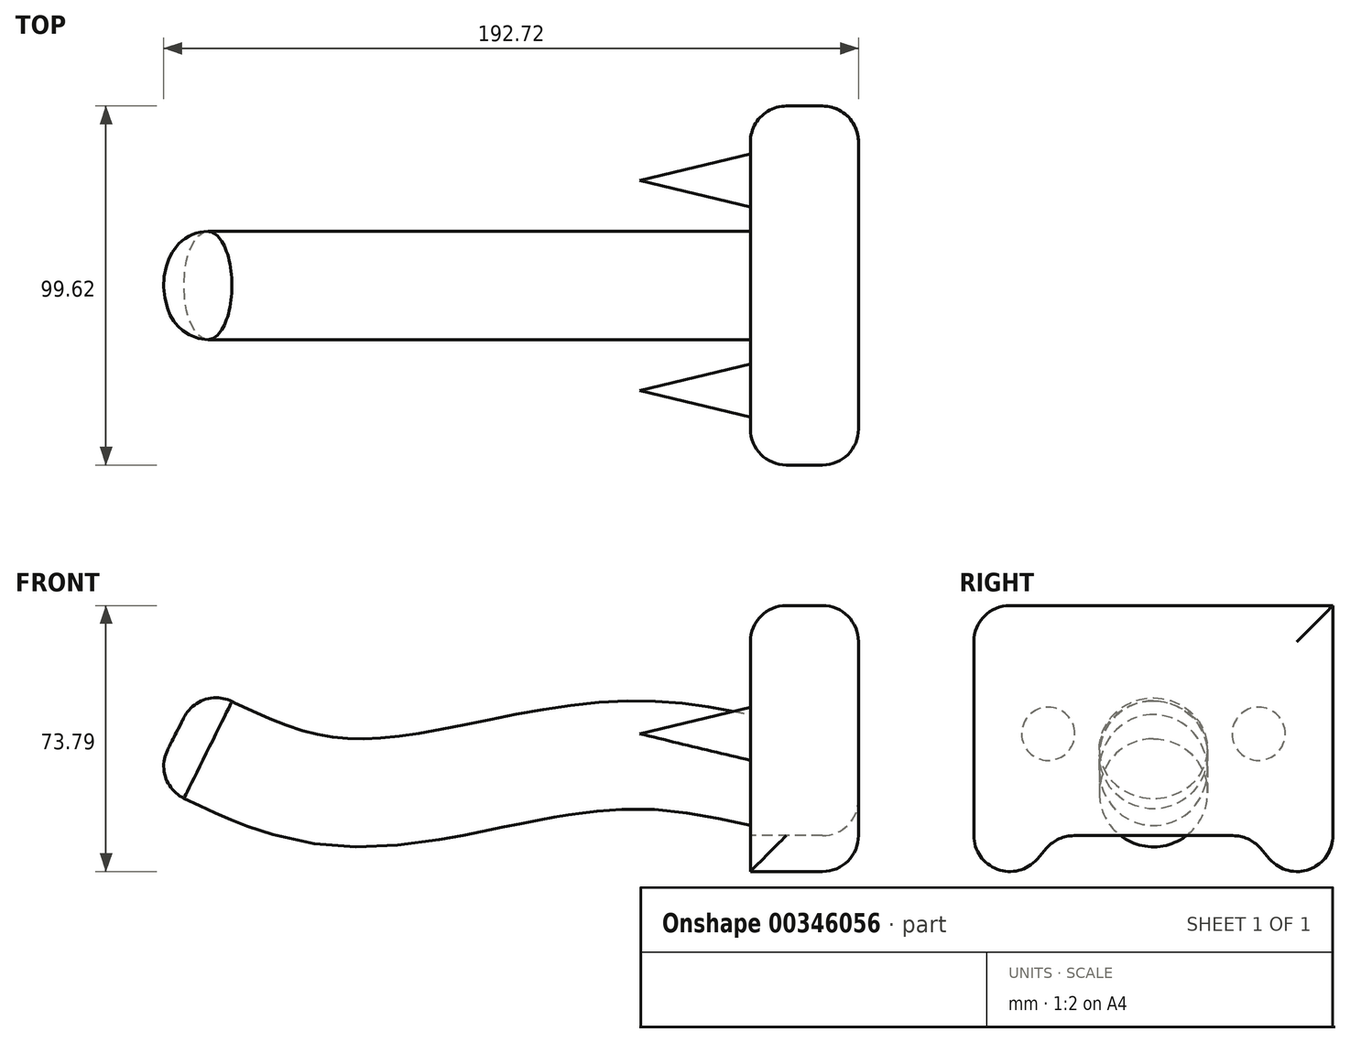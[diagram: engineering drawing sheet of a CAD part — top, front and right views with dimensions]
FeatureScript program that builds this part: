
annotation { "Feature Type Name" : "Feature", "Feature Type Description" : "" }
export const myFeature = defineFeature(function(context is Context, id is Id, definition is map)
    precondition{}
    {
        {
            var Q0;
            Q0=qCreatedBy(makeId("Right.planeOp"),FACE);
            var sketch = newSketch(context, id + "F0", { "sketchPlane" : qUnion([Q0])});
            skLineSegment(sketch, "E0", {"start": v(0, -28.27) * mm, "end": v(26.56, -28.27) * mm});
            skLineSegment(sketch, "E1", {"start": v(26.56, -28.27) * mm, "end": v(49.8, -54.84) * mm});
            skLineSegment(sketch, "E2", {"start": v(49.8, -54.84) * mm, "end": v(49.8, 35.57) * mm});
            skLineSegment(sketch, "E3", {"start": v(49.8, 35.57) * mm, "end": v(0, 35.57) * mm});
            skLineSegment(sketch, "E4.MirrorCS", {"start": v(0, -28.27) * mm, "end": v(-26.56, -28.27) * mm});
            skLineSegment(sketch, "E5.MirrorCS", {"start": v(-49.8, 35.57) * mm, "end": v(0, 35.57) * mm});
            skLineSegment(sketch, "E6.MirrorCS", {"start": v(-26.56, -28.27) * mm, "end": v(-49.8, -54.84) * mm});
            skLineSegment(sketch, "E7.MirrorCS", {"start": v(-49.8, -54.84) * mm, "end": v(-49.8, 35.57) * mm});
            skSolve(sketch);
        }
        {
            var Q0;
            Q0=makeQuery(id+"F0.imprint","IMPRINT",FACE,{"disambiguationData":[TD([[makeQuery(id+"F0.imprint","IMPRINT",EDGE,{"derivedFrom":sQuery(id+"F0.wireOp",EDGE,"E0")}),1.0]])]});
            extrude(context, id + "F1", {"entities" : qUnion([Q0]), "depth" : 30 * mm});
        }
        {
            var Q0;
            Q0=qCreatedBy(makeId("Front.planeOp"),FACE);
            var sketch = newSketch(context, id + "F2", { "sketchPlane" : qUnion([Q0])});
            skFitSpline(sketch, "E8", {"points": [v(11.8, -12.91) * mm, v(-35.42, -5.9) * mm, v(-90.03, -14.76) * mm, v(-125.09, -14.4) * mm, v(-159.4, 0) * mm], "startDerivative": vector(-174.02, 43.3) * mm, "endDerivative": vector(-148.88, 75.43) * mm});
            skSolve(sketch);
        }
        {
            var Q0;
            Q0=sQuery(id+"F2.wireOp",VERTEX,"E8.4.internal");
            var Q1;
            Q1=sQuery(id+"F2.wireOp",EDGE,"E8");
            cPlane(context, id + "F3", {"entities" : qUnion([Q0, Q1]), "cplaneType" : CPlaneType.CURVE_POINT, "offset" : 25 * mm, "width" : 150 * mm, "height" : 150 * mm});
        }
        {
            var Q0;
            Q0=qCreatedBy(id+"F3.planeOp",FACE);
            var sketch = newSketch(context, id + "F4", { "sketchPlane" : qUnion([Q0])});
            skPoint(sketch, "E9.0", {"position": v(0, -72.05) * mm});
            skCircle(sketch, "E10", {"center": v(0, -72.05) * mm, "radius": 15 * mm});
            skSolve(sketch);
        }
        {
            var Q0;
            Q0=makeQuery(id+"F4.imprint","IMPRINT",FACE,{"disambiguationData":[TD([[makeQuery(id+"F4.imprint","IMPRINT",EDGE,{"derivedFrom":sQuery(id+"F4.wireOp",EDGE,"E10")}),1.0]])]});
            var Q1;
            Q1=sQuery(id+"F2.wireOp",EDGE,"E8");
            sweep(context, id + "F5", {"operationType" : NewBodyOperationType.ADD, "profiles" : qUnion([Q0]), "path" : qUnion([Q1])});
        }
        {
            var Q0;
            Q0=qCreatedBy(makeId("Top.planeOp"),FACE);
            var sketch = newSketch(context, id + "F6", { "sketchPlane" : qUnion([Q0])});
            skLineSegment(sketch, "E11.0", {"start": v(0, 26.56) * mm, "end": v(0, 49.8) * mm});
            skLineSegment(sketch, "E12.0", {"start": v(0, 26.56) * mm, "end": v(0, -26.56) * mm});
            skLineSegment(sketch, "E13", {"start": v(0, 29.18) * mm, "end": v(-30.72, 29.18) * mm});
            skLineSegment(sketch, "E14", {"start": v(-30.72, 29.18) * mm, "end": v(0, 36.56) * mm});
            skLineSegment(sketch, "E15", {"start": v(0, 36.56) * mm, "end": v(0, 29.18) * mm});
            skSolve(sketch);
        }
        {
            var Q0;
            Q0=makeQuery(id+"F6.imprint","IMPRINT",FACE,{"disambiguationData":[TD([[makeQuery(id+"F6.imprint","IMPRINT",EDGE,{"derivedFrom":sQuery(id+"F6.wireOp",EDGE,"E13")}),-1.0]])]});
            var Q1;
            Q1=sQuery(id+"F6.wireOp",EDGE,"E13");
            revolve(context, id + "F7", {"operationType" : NewBodyOperationType.ADD, "entities" : qUnion([Q0]), "axis" : qUnion([Q1]), "revolveType" : RevolveType.FULL});
        }
        {
            var Q0;
            Q0=makeQuery(id+"F1.opExtrude","SWEPT_BODY",BODY,{"disambiguationData":[OSD([sQuery(id+"F0.wireOp",EDGE,"E0"),sQuery(id+"F0.wireOp",EDGE,"E1"),sQuery(id+"F0.wireOp",EDGE,"E2"),sQuery(id+"F0.wireOp",EDGE,"E3"),sQuery(id+"F0.wireOp",EDGE,"E4.MirrorCS"),sQuery(id+"F0.wireOp",EDGE,"E5.MirrorCS"),sQuery(id+"F0.wireOp",EDGE,"E6.MirrorCS"),sQuery(id+"F0.wireOp",EDGE,"E7.MirrorCS")])]});
            var Q1;
            Q1=qCreatedBy(makeId("Front.planeOp"),FACE);
            mirror(context, id + "F8", {"operationType" : NewBodyOperationType.ADD, "entities" : qUnion([Q0]), "mirrorPlane" : qUnion([Q1])});
        }
        {
            var Q0;
            Q0=makeQuery(id+"F5.opSweep","CAP_EDGE",EDGE,{"disambiguationData":[OSD([sQuery(id+"F2.wireOp",VERTEX,"E8.end"),sQuery(id+"F4.wireOp",EDGE,"E10")])],"isStart":true});
            var Q1;
            Q1=makeQuery(id+"F1.opExtrude","SWEPT_EDGE",EDGE,{"disambiguationData":[OSD([sQuery(id+"F0.wireOp",EDGE,"E5.MirrorCS"),sQuery(id+"F0.wireOp",EDGE,"E7.MirrorCS")])]});
            var Q2;
            Q2=makeQuery(id+"F1.opExtrude","CAP_EDGE",EDGE,{"disambiguationData":[OSD([sQuery(id+"F0.wireOp",EDGE,"E7.MirrorCS")])],"isStart":true});
            var Q3;
            Q3=makeQuery(id+"F1.opExtrude","CAP_EDGE",EDGE,{"disambiguationData":[OSD([sQuery(id+"F0.wireOp",EDGE,"E3"),sQuery(id+"F0.wireOp",EDGE,"E5.MirrorCS")])],"isStart":true});
            var Q4;
            Q4=makeQuery(id+"F1.opExtrude","CAP_EDGE",EDGE,{"disambiguationData":[OSD([sQuery(id+"F0.wireOp",EDGE,"E2")])],"isStart":true});
            var Q5;
            Q5=makeQuery(id+"F1.opExtrude","CAP_EDGE",EDGE,{"disambiguationData":[OSD([sQuery(id+"F0.wireOp",EDGE,"E7.MirrorCS")])],"isStart":false});
            var Q6;
            Q6=makeQuery(id+"F1.opExtrude","CAP_EDGE",EDGE,{"disambiguationData":[OSD([sQuery(id+"F0.wireOp",EDGE,"E2")])],"isStart":false});
            var Q7;
            Q7=makeQuery(id+"F1.opExtrude","CAP_EDGE",EDGE,{"disambiguationData":[OSD([sQuery(id+"F0.wireOp",EDGE,"E3"),sQuery(id+"F0.wireOp",EDGE,"E5.MirrorCS")])],"isStart":false});
            var Q8;
            Q8=makeQuery(id+"F1.opExtrude","CAP_EDGE",EDGE,{"disambiguationData":[OSD([sQuery(id+"F0.wireOp",EDGE,"E0"),sQuery(id+"F0.wireOp",EDGE,"E4.MirrorCS")])],"isStart":false});
            var Q9;
            Q9=makeQuery(id+"F1.opExtrude","CAP_EDGE",EDGE,{"disambiguationData":[OSD([sQuery(id+"F0.wireOp",EDGE,"E6.MirrorCS")])],"isStart":false});
            var Q10;
            Q10=makeQuery(id+"F1.opExtrude","CAP_EDGE",EDGE,{"disambiguationData":[OSD([sQuery(id+"F0.wireOp",EDGE,"E1")])],"isStart":false});
            var Q11;
            Q11=makeQuery(id+"F1.opExtrude","SWEPT_EDGE",EDGE,{"disambiguationData":[OSD([sQuery(id+"F0.wireOp",EDGE,"E4.MirrorCS"),sQuery(id+"F0.wireOp",EDGE,"E6.MirrorCS")])]});
            var Q12;
            Q12=makeQuery(id+"F1.opExtrude","SWEPT_EDGE",EDGE,{"disambiguationData":[OSD([sQuery(id+"F0.wireOp",EDGE,"E0"),sQuery(id+"F0.wireOp",EDGE,"E1")])]});
            var Q13;
            Q13=makeQuery(id+"F1.opExtrude","SWEPT_EDGE",EDGE,{"disambiguationData":[OSD([sQuery(id+"F0.wireOp",EDGE,"E1"),sQuery(id+"F0.wireOp",EDGE,"E2")])]});
            var Q14;
            Q14=makeQuery(id+"F1.opExtrude","SWEPT_EDGE",EDGE,{"disambiguationData":[OSD([sQuery(id+"F0.wireOp",EDGE,"E6.MirrorCS"),sQuery(id+"F0.wireOp",EDGE,"E7.MirrorCS")])]});
            fillet(context, id + "F9", {"entities" : qUnion([Q0, Q1, Q2, Q3, Q4, Q5, Q6, Q7, Q8, Q9, Q10, Q11, Q12, Q13, Q14]), "radius" : 10 * mm, "tangentPropagation" : true, "allowEdgeOverflow" : false});
        }
    });
